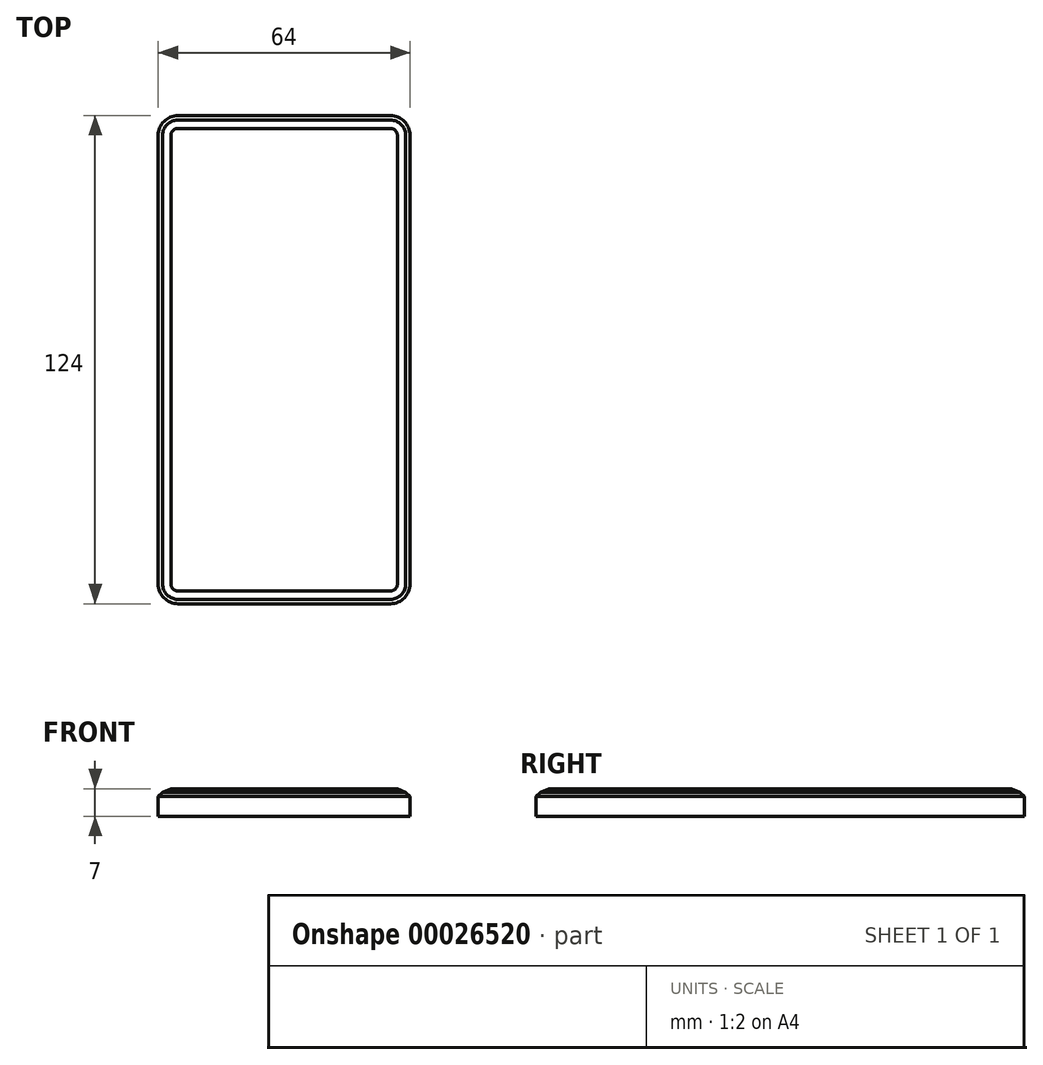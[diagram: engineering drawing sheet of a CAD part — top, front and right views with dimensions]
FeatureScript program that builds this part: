
annotation { "Feature Type Name" : "Feature", "Feature Type Description" : "" }
export const myFeature = defineFeature(function(context is Context, id is Id, definition is map)
    precondition{}
    {
        {
            var Q0;
            Q0=qCreatedBy(makeId("Top.planeOp"),FACE);
            var sketch = newSketch(context, id + "F0", { "sketchPlane" : qUnion([Q0])});
            skLineSegment(sketch, "E0.rect.bottom", {"start": v(-32, 62) * mm, "end": v(32, 62) * mm});
            skLineSegment(sketch, "E0.rect.top", {"start": v(-32, -62) * mm, "end": v(32, -62) * mm});
            skLineSegment(sketch, "E0.rect.left", {"start": v(-32, 62) * mm, "end": v(-32, -62) * mm});
            skLineSegment(sketch, "E0.rect.right", {"start": v(32, 62) * mm, "end": v(32, -62) * mm});
            skPoint(sketch, "E0.rect.middle", {"position": v(0, 0) * mm});
            skSolve(sketch);
        }
        {
            var Q0;
            Q0 = qSketchRegion(id + "F0", true);
            extrude(context, id + "F1", {"entities" : qUnion([Q0]), "depth" : 7 * mm});
        }
        {
            var Q0;
            Q0=makeQuery(id+"F1.opExtrude","SWEPT_EDGE",EDGE,{"disambiguationData":[OSD([sQuery(id+"F0.wireOp",EDGE,"E0.rect.bottom"),sQuery(id+"F0.wireOp",EDGE,"E0.rect.left")])]});
            var Q1;
            Q1=makeQuery(id+"F1.opExtrude","SWEPT_EDGE",EDGE,{"disambiguationData":[OSD([sQuery(id+"F0.wireOp",EDGE,"E0.rect.top"),sQuery(id+"F0.wireOp",EDGE,"E0.rect.left")])]});
            var Q2;
            Q2=makeQuery(id+"F1.opExtrude","SWEPT_EDGE",EDGE,{"disambiguationData":[OSD([sQuery(id+"F0.wireOp",EDGE,"E0.rect.bottom"),sQuery(id+"F0.wireOp",EDGE,"E0.rect.right")])]});
            var Q3;
            Q3=makeQuery(id+"F1.opExtrude","SWEPT_EDGE",EDGE,{"disambiguationData":[OSD([sQuery(id+"F0.wireOp",EDGE,"E0.rect.top"),sQuery(id+"F0.wireOp",EDGE,"E0.rect.right")])]});
            fillet(context, id + "F2", {"entities" : qUnion([Q0, Q1, Q2, Q3]), "radius" : 5 * mm, "tangentPropagation" : true, "allowEdgeOverflow" : false});
        }
        {
            var Q0;
            Q0=makeQuery(id+"F1.opExtrude","CAP_EDGE",EDGE,{"disambiguationData":[OSD([sQuery(id+"F0.wireOp",EDGE,"E0.rect.right")])],"isStart":false});
            var Q1;
            Q1=makeQuery(id+"F1.opExtrude","CAP_FACE",FACE,{"disambiguationData":[OSD([sQuery(id+"F0.wireOp",EDGE,"E0.rect.bottom"),sQuery(id+"F0.wireOp",EDGE,"E0.rect.top"),sQuery(id+"F0.wireOp",EDGE,"E0.rect.left"),sQuery(id+"F0.wireOp",EDGE,"E0.rect.right")])],"isStart":false});
            var Q2;
            Q2=makeQuery(id+"F1.opExtrude","CAP_EDGE",EDGE,{"disambiguationData":[OSD([sQuery(id+"F0.wireOp",EDGE,"E0.rect.left")])],"isStart":false});
            var Q3;
            Q3=makeQuery(id+"F1.opExtrude","CAP_EDGE",EDGE,{"disambiguationData":[OSD([sQuery(id+"F0.wireOp",EDGE,"E0.rect.bottom")])],"isStart":false});
            var Q4;
            Q4=makeQuery(id+"F1.opExtrude","CAP_EDGE",EDGE,{"disambiguationData":[OSD([sQuery(id+"F0.wireOp",EDGE,"E0.rect.top")])],"isStart":false});
            chamfer(context, id + "F3", {"entities" : qUnion([Q0, Q1, Q2, Q3, Q4]), "width" : 2 * mm, "tangentPropagation" : true});
        }
        {
            var Q0;
            Q0=makeQuery(id+"F1.opExtrude","CAP_FACE",FACE,{"disambiguationData":[OSD([sQuery(id+"F0.wireOp",EDGE,"E0.rect.bottom"),sQuery(id+"F0.wireOp",EDGE,"E0.rect.top"),sQuery(id+"F0.wireOp",EDGE,"E0.rect.left"),sQuery(id+"F0.wireOp",EDGE,"E0.rect.right")])],"isStart":false});
            chamfer(context, id + "F4", {"entities" : qUnion([Q0]), "width" : 3 * mm, "tangentPropagation" : true});
        }
    });
